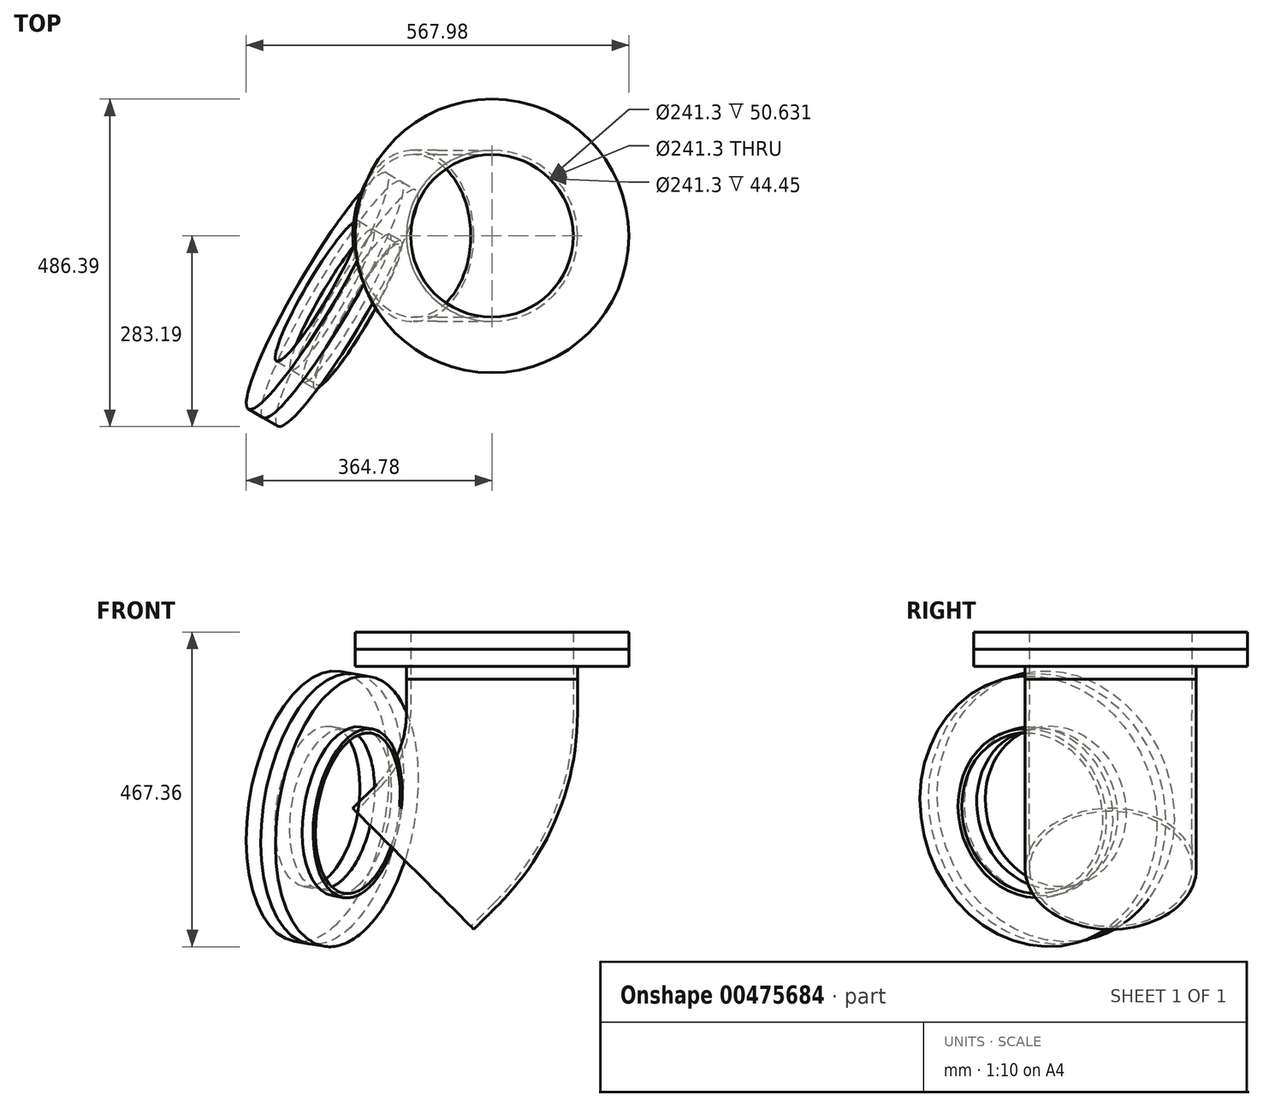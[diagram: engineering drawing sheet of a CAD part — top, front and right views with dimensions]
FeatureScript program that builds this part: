
annotation { "Feature Type Name" : "Feature", "Feature Type Description" : "" }
export const myFeature = defineFeature(function(context is Context, id is Id, definition is map)
    precondition{}
    {
        {
            var Q0;
            Q0=qCreatedBy(makeId("Top.planeOp"),FACE);
            var sketch = newSketch(context, id + "F0", { "sketchPlane" : qUnion([Q0])});
            skCircle(sketch, "E0", {"center": v(0, 0) * mm, "radius": 120.65 * mm});
            skCircle(sketch, "E1", {"center": v(0, 0) * mm, "radius": 127 * mm});
            skSolve(sketch);
        }
        {
            var Q0;
            Q0=makeQuery(id+"F0.imprint","IMPRINT",FACE,{"disambiguationData":[TD([[makeQuery(id+"F0.imprint","IMPRINT",EDGE,{"derivedFrom":sQuery(id+"F0.wireOp",EDGE,"E0")}),-1.0]])]});
            extrude(context, id + "F1", {"entities" : qUnion([Q0]), "depth" : 19.05 * mm});
        }
        {
            var Q0;
            Q0=makeQuery(id+"F1.opExtrude","CAP_FACE",FACE,{"disambiguationData":[OSD([sQuery(id+"F0.wireOp",EDGE,"E0"),sQuery(id+"F0.wireOp",EDGE,"E1")])],"isStart":false});
            var sketch = newSketch(context, id + "F2", { "sketchPlane" : qUnion([Q0])});
            skCircle(sketch, "E2", {"center": v(0, 0) * mm, "radius": 203.2 * mm});
            skSolve(sketch);
        }
        {
            var Q0;
            Q0=makeQuery(id+"F2.imprint","IMPRINT",FACE,{"disambiguationData":[TD([[makeQuery(id+"F2.imprint","IMPRINT",EDGE,{"derivedFrom":sQuery(id+"F2.wireOp",EDGE,"E2")}),1.0]])]});
            var Q1;
            Q1=makeQuery(id+"F2.imprint","IMPRINT",FACE,{"disambiguationData":[TD([[makeQuery(id+"F2.imprint","IMPRINT",EDGE,{"derivedFrom":makeQuery(id+"F1.opExtrude","CAP_EDGE",EDGE,{"disambiguationData":[OSD([sQuery(id+"F0.wireOp",EDGE,"E0")])],"isStart":false})}),-1.0]])]});
            extrude(context, id + "F3", {"entities" : qUnion([Q0, Q1]), "operationType" : NewBodyOperationType.ADD, "depth" : 25.4 * mm});
        }
        {
            var Q0;
            Q0=qCreatedBy(makeId("Front.planeOp"),FACE);
            var sketch = newSketch(context, id + "F4", { "sketchPlane" : qUnion([Q0])});
            skLineSegment(sketch, "E3", {"start": v(0, 0) * mm, "end": v(0, -50.63) * mm});
            skLineSegment(sketch, "E4", {"start": v(-80.94, -246.04) * mm, "end": v(-116.74, -281.84) * mm});
            skPoint(sketch, "E5.visualSharp", {"position": v(0, -165.1) * mm});
            skArc(sketch, "E5.filletArc", {"start": v(-80.94, -246.04) * mm, "mid": v(-21.04, -156.39) * mm, "end": v(0, -50.63) * mm});
            skSolve(sketch);
        }
        {
            var Q0;
            Q0=makeQuery(id+"F1.opExtrude","CAP_FACE",FACE,{"disambiguationData":[OSD([sQuery(id+"F0.wireOp",EDGE,"E0"),sQuery(id+"F0.wireOp",EDGE,"E1")])],"isStart":true});
            var Q1;
            Q1=sQuery(id+"F4.wireOp",EDGE,"E5.filletArc");
            var Q2;
            Q2=sQuery(id+"F4.wireOp",EDGE,"E4");
            var Q3;
            Q3=sQuery(id+"F4.wireOp",EDGE,"E3");
            sweep(context, id + "F5", {"profiles" : qUnion([Q0]), "path" : qUnion([Q1, Q2, Q3])});
        }
        {
            var Q0;
            Q0=makeQuery(id+"F5.opSweep","CAP_FACE",FACE,{"disambiguationData":[OSD([sQuery(id+"F0.wireOp",EDGE,"E0"),sQuery(id+"F0.wireOp",EDGE,"E1"),sQuery(id+"F4.wireOp",VERTEX,"E4.end")])],"isStart":false});
            var sketch = newSketch(context, id + "F6", { "sketchPlane" : qUnion([Q0])});
            skPoint(sketch, "E6", {"position": v(116.74, 0) * mm});
            skLineSegment(sketch, "E7", {"start": v(116.74, 0) * mm, "end": v(116.74, 343.85) * mm, "construction": true});
            skSolve(sketch);
        }
        {
            var Q0;
            Q0=makeQuery(id+"F1.opExtrude","SWEPT_BODY",BODY,{"disambiguationData":[OSD([sQuery(id+"F0.wireOp",EDGE,"E0"),sQuery(id+"F0.wireOp",EDGE,"E1")])]});
            var Q1;
            Q1=qCreatedBy(makeId("Origin.pointOp"),VERTEX);
            var Q2;
            Q2=sQuery(id+"F6.wireOp",VERTEX,"E6");
            transform(context, id + "F7", {"entities" : qUnion([Q0]), "transformType" : TransformType.TRANSLATION_ENTITY, "oppositeDirectionEntity" : false, "transformLine" : qUnion([Q1, Q2]), "makeCopy" : true});
        }
        {
            var Q0;
            Q0=makeQuery(id+"F7.opPattern","COPY",BODY,{"derivedFrom":makeQuery(id+"F1.opExtrude","SWEPT_BODY",BODY,{"disambiguationData":[OSD([sQuery(id+"F0.wireOp",EDGE,"E0"),sQuery(id+"F0.wireOp",EDGE,"E1")])]}),"instanceName":"1"});
            var Q1;
            Q1=sQuery(id+"F6.wireOp",VERTEX,"E6");
            var Q2;
            Q2=sQuery(id+"F6.wireOp",EDGE,"E7");
            transform(context, id + "F8", {"entities" : qUnion([Q0]), "transformType" : TransformType.ROTATION, "transformAxis" : qUnion([Q2]), "angle" : 135 * degree, "makeCopy" : false});
        }
        {
            var Q0;
            Q0=makeQuery(id+"F3.opExtrude","CAP_FACE",FACE,{"disambiguationData":[OSD([sQuery(id+"F0.wireOp",EDGE,"E0"),sQuery(id+"F2.wireOp",EDGE,"E2")])],"isStart":false});
            extrude(context, id + "F9", {"entities" : qUnion([Q0]), "depth" : 25.4 * mm});
        }
        {
            var Q0;
            Q0=makeQuery(id+"F7.opPattern","COPY",FACE,{"derivedFrom":makeQuery(id+"F3.opExtrude","CAP_FACE",FACE,{"disambiguationData":[OSD([sQuery(id+"F0.wireOp",EDGE,"E0"),sQuery(id+"F2.wireOp",EDGE,"E2")])],"isStart":false}),"instanceName":"1"});
            extrude(context, id + "F10", {"entities" : qUnion([Q0]), "depth" : 25.4 * mm});
        }
    });
